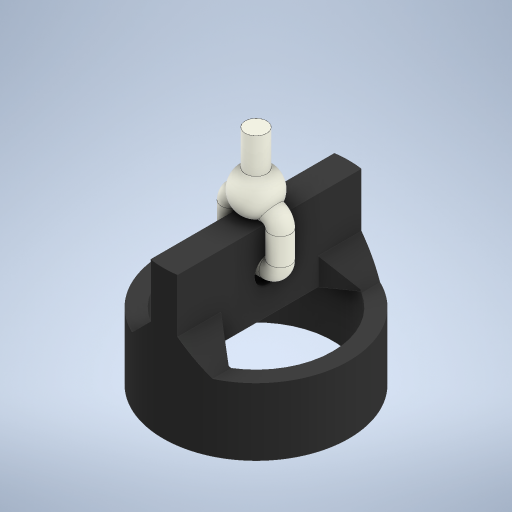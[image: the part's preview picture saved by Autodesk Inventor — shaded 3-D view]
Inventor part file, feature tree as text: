
AUTODESK INVENTOR PART (.ipt)
format: ipt  version: 2024.3 (Build 283343000, 343)  size: 368,128 bytes
history: native  units: mm
features: sketch x5, extrude x4, chamfer x2, projected_geometry x2, other x1, sweep x1, plane x1, revolve x1
ambient origin geometry x8: Origin, YZ Plane, XZ Plane, XY Plane, X Axis, Y Axis, Z Axis, Center Point
bodies: Body1 (feature_tree)
feature tree (17):
  other  "솔리드1"
  extrude  "돌출1"  Depth=6.9mm
  extrude  "돌출2"  Depth=1.0mm
  chamfer  "모따기1"  Distance=3.0mm
  chamfer  "모따기2"  Distance=1.0mm Angle=45.0deg
  extrude  "돌출4"  Depth=1.0mm
  sweep  "Sweep1"
  plane  "Work Plane1"
  revolve  "Revolution1"  [1 undecoded]
  extrude  "Extrusion5"  Depth=0.8mm
  sketch  "스케치5"
  projected_geometry  "투영된 루프3"
  sketch  "Sketch6"  dims[d0=5.7mm d1=6.9mm]
  projected_geometry  "Projected Loop4"
  sketch  "Sketch7"  dims[d2=2.5mm d3=0.0mm d4=1.0mm d5=3.0mm d6=0.0mm d7=1.0mm d8=2.0mm d9=45.0deg]
  sketch  "Sketch8"  dims[d12=1.0mm d13=2.0mm d14=45.0deg d15=1.0mm]
  sketch  "Sketch9"  dims[d16=1.5mm d17=3.0mm d18=0.0mm d21=0.4mm d22=0.78mm d23=0.0mm d24=0.0mm d25=0.8mm d26=1.6mm d27=90.0deg d28=0.8mm d29=2.0mm d30=0.0mm]
note: 1 required parameter value undecoded (feature->parameter linkage not recoverable at this tier; creation-order binding heuristic only, values carry confidence <= 0.55)
